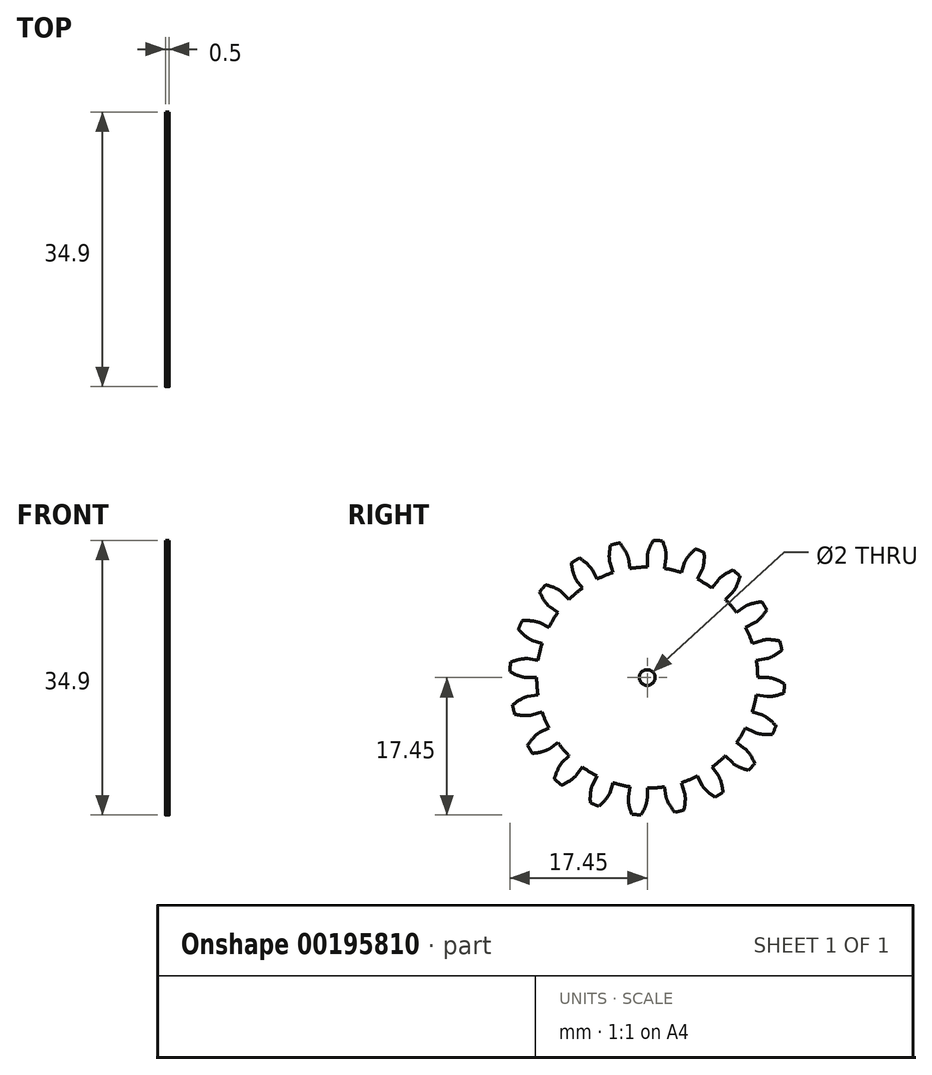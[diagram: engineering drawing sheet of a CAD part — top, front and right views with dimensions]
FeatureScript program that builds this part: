
annotation { "Feature Type Name" : "Feature", "Feature Type Description" : "" }
export const myFeature = defineFeature(function(context is Context, id is Id, definition is map)
    precondition{}
    {
        {
            assignVariable(context, id + "F0", {"name" : "NumberTeeth", "anyValue" : 20});
        }
        {
            assignVariable(context, id + "F1", {"name" : "GearThickness", "anyValue" : .5});
        }
        {
            var Q0;
            Q0=qCreatedBy(makeId("Right.planeOp"),FACE);
            var sketch = newSketch(context, id + "F2", { "sketchPlane" : qUnion([Q0])});
            skCircle(sketch, "E0", {"center": v(0, 0) * mm, "radius": 14.04 * mm});
            skCircle(sketch, "E1", {"center": v(0, 0) * mm, "radius": 15.37 * mm, "construction": true});
            skCircle(sketch, "E2", {"center": v(0, 0) * mm, "radius": 15.88 * mm, "construction": true});
            skCircle(sketch, "E3", {"center": v(0, 0) * mm, "radius": 17.46 * mm});
            skLineSegment(sketch, "E4", {"start": v(0, 0) * mm, "end": v(-15.37, 0) * mm, "construction": true});
            skLineSegment(sketch, "E5.1.0", {"start": v(0, 0) * mm, "end": v(-15.35, 0.77) * mm, "construction": true});
            skLineSegment(sketch, "E5.2.0", {"start": v(0, 0) * mm, "end": v(-15.3, 1.53) * mm, "construction": true});
            skLineSegment(sketch, "E5.3.0", {"start": v(0, 0) * mm, "end": v(-15.2, 2.3) * mm, "construction": true});
            skLineSegment(sketch, "E5.4.0", {"start": v(0, 0) * mm, "end": v(-15.06, 3.05) * mm, "construction": true});
            skLineSegment(sketch, "E5.5.0", {"start": v(0, 0) * mm, "end": v(-14.9, 3.8) * mm, "construction": true});
            skLineSegment(sketch, "E5.6.0", {"start": v(0, 0) * mm, "end": v(-14.68, 4.54) * mm, "construction": true});
            skLineSegment(sketch, "E5.7.0", {"start": v(0, 0) * mm, "end": v(-14.44, 5.27) * mm, "construction": true});
            skLineSegment(sketch, "E5.8.0", {"start": v(0, 0) * mm, "end": v(-14.16, 5.99) * mm, "construction": true});
            skLineSegment(sketch, "E5.9.0", {"start": v(0, 0) * mm, "end": v(-13.84, 6.69) * mm, "construction": true});
            skLineSegment(sketch, "E5.10.0", {"start": v(0, 0) * mm, "end": v(-13.49, 7.37) * mm, "construction": true});
            skLineSegment(sketch, "E5.11.0", {"start": v(0, 0) * mm, "end": v(-13.1, 8.03) * mm, "construction": true});
            skLineSegment(sketch, "E5.12.0", {"start": v(0, 0) * mm, "end": v(-12.68, 8.68) * mm, "construction": true});
            skLineSegment(sketch, "E5.13.0", {"start": v(0, 0) * mm, "end": v(-12.24, 9.3) * mm, "construction": true});
            skLineSegment(sketch, "E5.14.0", {"start": v(0, 0) * mm, "end": v(-11.76, 9.9) * mm, "construction": true});
            skLineSegment(sketch, "E5.anchor2", {"start": v(0, 0) * mm, "end": v(-11.76, 9.9) * mm, "construction": true});
            skLineSegment(sketch, "E6", {"start": v(-15.35, 0.77) * mm, "end": v(-15.39, 0) * mm, "construction": true});
            skLineSegment(sketch, "E7", {"start": v(-15.3, 1.53) * mm, "end": v(-15.45, 0) * mm, "construction": true});
            skLineSegment(sketch, "E8", {"start": v(-15.2, 2.3) * mm, "end": v(-15.54, 0.02) * mm, "construction": true});
            skLineSegment(sketch, "E9", {"start": v(-14.9, 3.8) * mm, "end": v(-15.84, 0.08) * mm, "construction": true});
            skLineSegment(sketch, "E10", {"start": v(-14.68, 4.54) * mm, "end": v(-16.05, 0.14) * mm, "construction": true});
            skLineSegment(sketch, "E11", {"start": v(-14.44, 5.27) * mm, "end": v(-16.28, 0.22) * mm, "construction": true});
            skLineSegment(sketch, "E12", {"start": v(-14.16, 5.99) * mm, "end": v(-16.55, 0.32) * mm, "construction": true});
            skLineSegment(sketch, "E13", {"start": v(-13.84, 6.69) * mm, "end": v(-16.85, 0.46) * mm, "construction": true});
            skLineSegment(sketch, "E14", {"start": v(-13.49, 7.37) * mm, "end": v(-17.17, 0.62) * mm, "construction": true});
            skLineSegment(sketch, "E15", {"start": v(-13.1, 8.03) * mm, "end": v(-17.52, 0.83) * mm, "construction": true});
            skLineSegment(sketch, "E16", {"start": v(-15.06, 3.05) * mm, "end": v(-15.67, 0.04) * mm, "construction": true});
            skLineSegment(sketch, "E17", {"start": v(-12.68, 8.68) * mm, "end": v(-17.9, 1.07) * mm, "construction": true});
            skLineSegment(sketch, "E18", {"start": v(-12.24, 9.3) * mm, "end": v(-18.28, 1.35) * mm, "construction": true});
            skLineSegment(sketch, "E19", {"start": v(-11.76, 9.9) * mm, "end": v(-18.69, 1.67) * mm, "construction": true});
            skLineSegment(sketch, "E20", {"start": v(0, 0) * mm, "end": v(-15.32, 1.2) * mm, "construction": true});
            skLineSegment(sketch, "E21", {"start": v(-14.04, 0) * mm, "end": v(-15.37, 0) * mm});
            skLineSegment(sketch, "E22.MirrorCS", {"start": v(-13.87, 2.2) * mm, "end": v(-15.18, 2.4) * mm});
            skFitSpline(sketch, "E23", {"points": [v(-15.37, 0) * mm, v(-15.39, 0) * mm, v(-15.45, 0) * mm, v(-15.54, 0.02) * mm, v(-15.67, 0.04) * mm, v(-15.84, 0.08) * mm, v(-16.05, 0.14) * mm, v(-16.28, 0.22) * mm, v(-16.55, 0.32) * mm, v(-16.85, 0.46) * mm, v(-17.17, 0.62) * mm, v(-17.52, 0.83) * mm, v(-17.9, 1.07) * mm, v(-18.28, 1.35) * mm, v(-18.69, 1.67) * mm], "startDerivative": vector(-0.82, 0) * mm, "endDerivative": vector(-1.2, 1) * mm});
            skLineSegment(sketch, "E24", {"start": v(-18.69, 1.67) * mm, "end": v(-19.04, 1.97) * mm, "construction": true});
            skFitSpline(sketch, "E25.MirrorCS", {"points": [v(-15.18, 2.4) * mm, v(-15.2, 2.4) * mm, v(-15.26, 2.41) * mm, v(-15.35, 2.41) * mm, v(-15.49, 2.41) * mm, v(-15.66, 2.4) * mm, v(-15.87, 2.37) * mm, v(-16.12, 2.33) * mm, v(-16.4, 2.27) * mm, v(-16.71, 2.18) * mm, v(-17.06, 2.07) * mm, v(-17.43, 1.92) * mm, v(-17.84, 1.74) * mm, v(-18.27, 1.53) * mm, v(-18.72, 1.27) * mm], "startDerivative": vector(-0.8, 0.13) * mm, "endDerivative": vector(-1.34, -0.8) * mm});
            skSolve(sketch);
        }
        {
            var Q0;
            {var subQ0=sQuery(id+"F2.wireOp",EDGE,"E0");var subQ27=makeQuery(id+"F2.imprint","INTERSECT",VERTEX,{"derivedFrom":[subQ0,sQuery(id+"F2.wireOp",EDGE,"10ea1024-8cf5-41f5-a75f-a634b86921f3.10.0")]});Q0=makeQuery(id+"F2.imprint","IMPRINT",FACE,{"disambiguationData":[TD([[makeQuery(id+"F2.imprint","IMPRINT",EDGE,{"disambiguationData":[TD([[subQ27,-1.0]])],"derivedFrom":subQ0}),1.0]])]});}
            var Q1;
            {var subQ0=sQuery(id+"F2.wireOp",EDGE,"10ea1024-8cf5-41f5-a75f-a634b86921f3.1.0");Q1=makeQuery(id+"F2.imprint","IMPRINT",FACE,{"disambiguationData":[TD([[makeQuery(id+"F2.imprint","IMPRINT",EDGE,{"derivedFrom":subQ0}),-1.0]])]});}
            var Q2;
            {var subQ7=sQuery(id+"F2.wireOp",EDGE,"10ea1024-8cf5-41f5-a75f-a634b86921f3.2.0");Q2=makeQuery(id+"F2.imprint","IMPRINT",FACE,{"disambiguationData":[TD([[makeQuery(id+"F2.imprint","IMPRINT",EDGE,{"derivedFrom":subQ7}),-1.0]])]});}
            var Q3;
            {var subQ8=sQuery(id+"F2.wireOp",EDGE,"10ea1024-8cf5-41f5-a75f-a634b86921f3.3.0");Q3=makeQuery(id+"F2.imprint","IMPRINT",FACE,{"disambiguationData":[TD([[makeQuery(id+"F2.imprint","IMPRINT",EDGE,{"derivedFrom":subQ8}),-1.0]])]});}
            var Q4;
            {var subQ2=sQuery(id+"F2.wireOp",EDGE,"10ea1024-8cf5-41f5-a75f-a634b86921f3.4.0");Q4=makeQuery(id+"F2.imprint","IMPRINT",FACE,{"disambiguationData":[TD([[makeQuery(id+"F2.imprint","IMPRINT",EDGE,{"derivedFrom":subQ2}),-1.0]])]});}
            var Q5;
            {var subQ8=sQuery(id+"F2.wireOp",EDGE,"10ea1024-8cf5-41f5-a75f-a634b86921f3.5.0");Q5=makeQuery(id+"F2.imprint","IMPRINT",FACE,{"disambiguationData":[TD([[makeQuery(id+"F2.imprint","IMPRINT",EDGE,{"derivedFrom":subQ8}),-1.0]])]});}
            var Q6;
            {var subQ3=sQuery(id+"F2.wireOp",EDGE,"10ea1024-8cf5-41f5-a75f-a634b86921f3.6.0");Q6=makeQuery(id+"F2.imprint","IMPRINT",FACE,{"disambiguationData":[TD([[makeQuery(id+"F2.imprint","IMPRINT",EDGE,{"derivedFrom":subQ3}),-1.0]])]});}
            var Q7;
            {var subQ0=sQuery(id+"F2.wireOp",EDGE,"10ea1024-8cf5-41f5-a75f-a634b86921f3.7.0");Q7=makeQuery(id+"F2.imprint","IMPRINT",FACE,{"disambiguationData":[TD([[makeQuery(id+"F2.imprint","IMPRINT",EDGE,{"derivedFrom":subQ0}),-1.0]])]});}
            var Q8;
            {var subQ5=sQuery(id+"F2.wireOp",EDGE,"10ea1024-8cf5-41f5-a75f-a634b86921f3.8.0");Q8=makeQuery(id+"F2.imprint","IMPRINT",FACE,{"disambiguationData":[TD([[makeQuery(id+"F2.imprint","IMPRINT",EDGE,{"derivedFrom":subQ5}),-1.0]])]});}
            var Q9;
            {var subQ1=sQuery(id+"F2.wireOp",EDGE,"10ea1024-8cf5-41f5-a75f-a634b86921f3.9.0");Q9=makeQuery(id+"F2.imprint","IMPRINT",FACE,{"disambiguationData":[TD([[makeQuery(id+"F2.imprint","IMPRINT",EDGE,{"derivedFrom":subQ1}),-1.0]])]});}
            var Q10;
            {var subQ5=sQuery(id+"F2.wireOp",EDGE,"10ea1024-8cf5-41f5-a75f-a634b86921f3.10.0");Q10=makeQuery(id+"F2.imprint","IMPRINT",FACE,{"disambiguationData":[TD([[makeQuery(id+"F2.imprint","IMPRINT",EDGE,{"derivedFrom":subQ5}),-1.0]])]});}
            var Q11;
            {var subQ8=sQuery(id+"F2.wireOp",EDGE,"10ea1024-8cf5-41f5-a75f-a634b86921f3.11.0");Q11=makeQuery(id+"F2.imprint","IMPRINT",FACE,{"disambiguationData":[TD([[makeQuery(id+"F2.imprint","IMPRINT",EDGE,{"derivedFrom":subQ8}),-1.0]])]});}
            var Q12;
            {var subQ2=sQuery(id+"F2.wireOp",EDGE,"10ea1024-8cf5-41f5-a75f-a634b86921f3.12.0");Q12=makeQuery(id+"F2.imprint","IMPRINT",FACE,{"disambiguationData":[TD([[makeQuery(id+"F2.imprint","IMPRINT",EDGE,{"derivedFrom":subQ2}),-1.0]])]});}
            var Q13;
            {var subQ3=sQuery(id+"F2.wireOp",EDGE,"10ea1024-8cf5-41f5-a75f-a634b86921f3.13.0");Q13=makeQuery(id+"F2.imprint","IMPRINT",FACE,{"disambiguationData":[TD([[makeQuery(id+"F2.imprint","IMPRINT",EDGE,{"derivedFrom":subQ3}),-1.0]])]});}
            var Q14;
            {var subQ0=sQuery(id+"F2.wireOp",EDGE,"10ea1024-8cf5-41f5-a75f-a634b86921f3.14.0");Q14=makeQuery(id+"F2.imprint","IMPRINT",FACE,{"disambiguationData":[TD([[makeQuery(id+"F2.imprint","IMPRINT",EDGE,{"derivedFrom":subQ0}),-1.0]])]});}
            var Q15;
            {var subQ6=sQuery(id+"F2.wireOp",EDGE,"10ea1024-8cf5-41f5-a75f-a634b86921f3.15.0");Q15=makeQuery(id+"F2.imprint","IMPRINT",FACE,{"disambiguationData":[TD([[makeQuery(id+"F2.imprint","IMPRINT",EDGE,{"derivedFrom":subQ6}),-1.0]])]});}
            var Q16;
            {var subQ5=sQuery(id+"F2.wireOp",EDGE,"10ea1024-8cf5-41f5-a75f-a634b86921f3.16.0");Q16=makeQuery(id+"F2.imprint","IMPRINT",FACE,{"disambiguationData":[TD([[makeQuery(id+"F2.imprint","IMPRINT",EDGE,{"derivedFrom":subQ5}),-1.0]])]});}
            var Q17;
            {var subQ7=sQuery(id+"F2.wireOp",EDGE,"10ea1024-8cf5-41f5-a75f-a634b86921f3.17.0");Q17=makeQuery(id+"F2.imprint","IMPRINT",FACE,{"disambiguationData":[TD([[makeQuery(id+"F2.imprint","IMPRINT",EDGE,{"derivedFrom":subQ7}),-1.0]])]});}
            var Q18;
            {var subQ5=sQuery(id+"F2.wireOp",EDGE,"10ea1024-8cf5-41f5-a75f-a634b86921f3.18.0");Q18=makeQuery(id+"F2.imprint","IMPRINT",FACE,{"disambiguationData":[TD([[makeQuery(id+"F2.imprint","IMPRINT",EDGE,{"derivedFrom":subQ5}),-1.0]])]});}
            var Q19;
            {var subQ8=sQuery(id+"F2.wireOp",EDGE,"10ea1024-8cf5-41f5-a75f-a634b86921f3.19.0");Q19=makeQuery(id+"F2.imprint","IMPRINT",FACE,{"disambiguationData":[TD([[makeQuery(id+"F2.imprint","IMPRINT",EDGE,{"derivedFrom":subQ8}),-1.0]])]});}
            var Q20;
            {var subQ8=sQuery(id+"F2.wireOp",EDGE,"E21");Q20=makeQuery(id+"F2.imprint","IMPRINT",FACE,{"disambiguationData":[TD([[makeQuery(id+"F2.imprint","IMPRINT",EDGE,{"derivedFrom":subQ8}),-1.0]])]});}
            extrude(context, id + "F3", {"entities" : qUnion([Q0, Q1, Q2, Q3, Q4, Q5, Q6, Q7, Q8, Q9, Q10, Q11, Q12, Q13, Q14, Q15, Q16, Q17, Q18, Q19, Q20]), "depth" : (getVariable(context, 'GearThickness')) * mm});
        }
        {
            var Q0;
            Q0=makeQuery(id+"F3.opExtrude","SWEPT_FACE",FACE,{"disambiguationData":[OSD([sQuery(id+"F2.wireOp",EDGE,"E25.MirrorCS")])]});
            var Q1;
            Q1=makeQuery(id+"F3.opExtrude","SWEPT_FACE",FACE,{"disambiguationData":[OSD([sQuery(id+"F2.wireOp",EDGE,"E23")])]});
            var Q2;
            Q2=makeQuery(id+"F3.opExtrude","SWEPT_FACE",FACE,{"disambiguationData":[OSD([sQuery(id+"F2.wireOp",EDGE,"E3")])]});
            var Q3;
            Q3=makeQuery(id+"F3.opExtrude","SWEPT_FACE",FACE,{"disambiguationData":[OSD([sQuery(id+"F2.wireOp",EDGE,"E22.MirrorCS")])]});
            var Q4;
            Q4=makeQuery(id+"F3.opExtrude","SWEPT_FACE",FACE,{"disambiguationData":[OSD([sQuery(id+"F2.wireOp",EDGE,"E21")])]});
            var Q5;
            Q5=makeQuery(id+"F3.opExtrude","SWEPT_FACE",FACE,{"disambiguationData":[OSD([sQuery(id+"F2.wireOp",EDGE,"E0")])]});
            circularPattern(context, id + "F4", {"faces" : qUnion([Q0, Q1, Q2, Q3, Q4]), "axis" : qUnion([Q5]), "angle" : 360 * degree, "instanceCount" : getVariable(context, 'NumberTeeth'), "equalSpace" : true, "patternType" : PatternType.FACE});
        }
        {
            var Q0;
            Q0=makeQuery(id+"F3.opExtrude","CAP_FACE",FACE,{"disambiguationData":[OSD([sQuery(id+"F2.wireOp",EDGE,"E0"),sQuery(id+"F2.wireOp",EDGE,"E3"),sQuery(id+"F2.wireOp",EDGE,"E21"),sQuery(id+"F2.wireOp",EDGE,"E22.MirrorCS"),sQuery(id+"F2.wireOp",EDGE,"E23"),sQuery(id+"F2.wireOp",EDGE,"E25.MirrorCS")])],"isStart":false});
            var sketch = newSketch(context, id + "F5", { "sketchPlane" : qUnion([Q0])});
            skCircle(sketch, "E26", {"center": v(0, 0) * mm, "radius": 1 * mm});
            skSolve(sketch);
        }
        {
            var Q0;
            Q0 = qSketchRegion(id + "F5", true);
            extrude(context, id + "F6", {"entities" : qUnion([Q0]), "operationType" : NewBodyOperationType.REMOVE, "endBound" : BoundingType.THROUGH_ALL, "oppositeDirection" : true, "depth" : 25.4 * mm});
        }
    });
